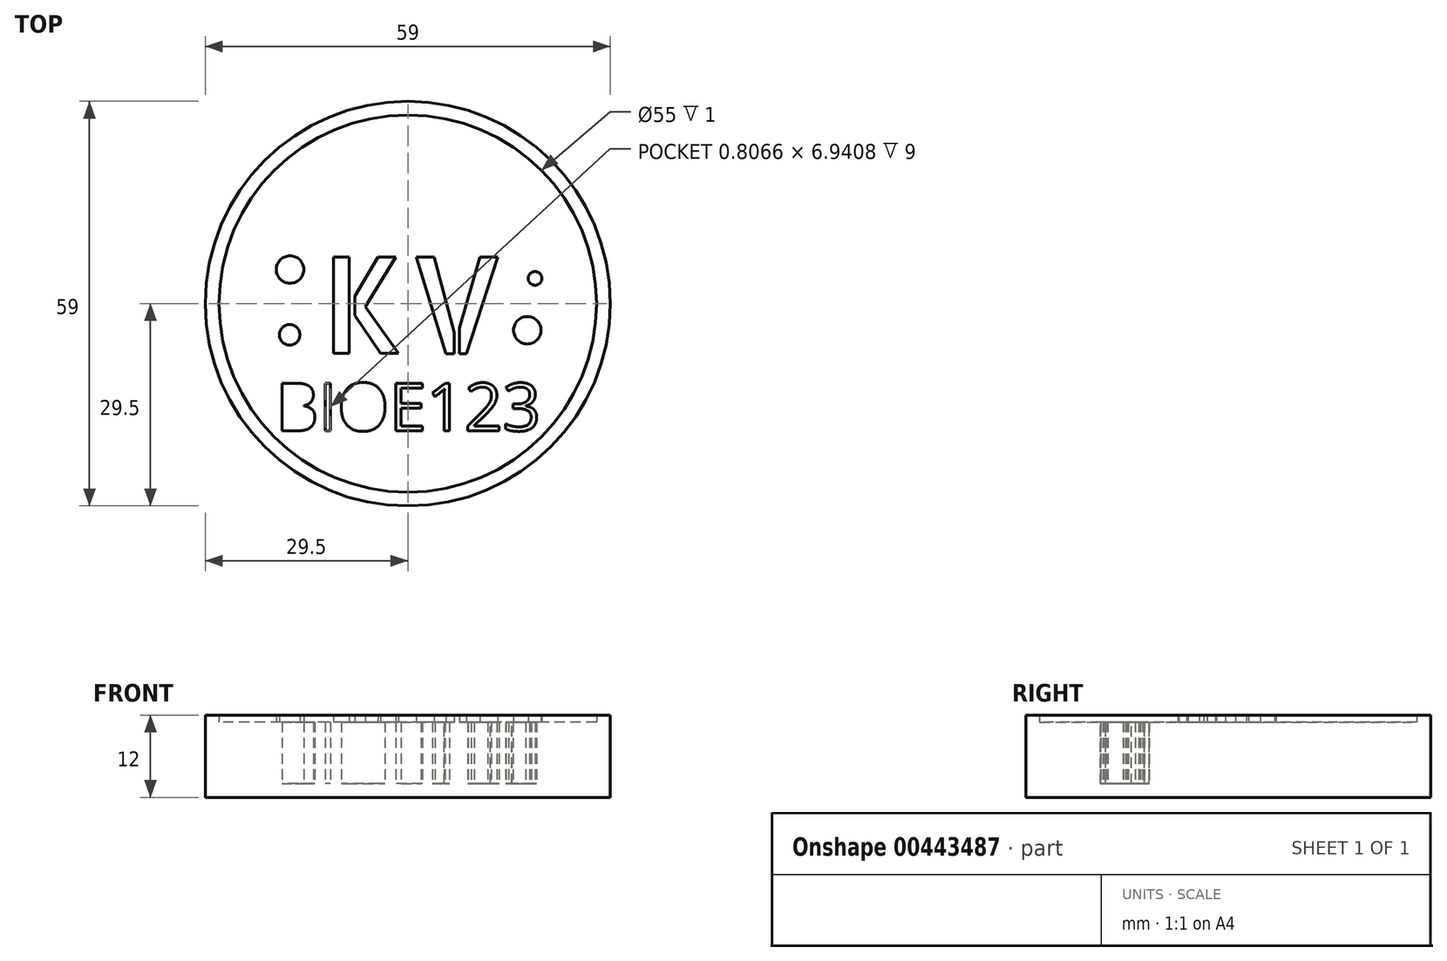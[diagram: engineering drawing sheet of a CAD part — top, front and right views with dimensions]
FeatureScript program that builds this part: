
annotation { "Feature Type Name" : "Feature", "Feature Type Description" : "" }
export const myFeature = defineFeature(function(context is Context, id is Id, definition is map)
    precondition{}
    {
        {
            var Q0;
            Q0=qCreatedBy(makeId("Top.planeOp"),FACE);
            var sketch = newSketch(context, id + "F0", { "sketchPlane" : qUnion([Q0])});
            skCircle(sketch, "E0", {"center": v(0, 0) * mm, "radius": 22.5 * mm});
            skCircle(sketch, "E1", {"center": v(0, 0) * mm, "radius": 27.5 * mm});
            skText(sketch, "E2", { "text": "KV", "fontName": "AllertaStencil-Regular.ttf"});
            skCircle(sketch, "E3", {"center": v(-17.22, -4.56) * mm, "radius": 1.5 * mm});
            skCircle(sketch, "E4", {"center": v(-17.16, 4.97) * mm, "radius": 2 * mm});
            skCircle(sketch, "E5", {"center": v(18.54, 3.68) * mm, "radius": 1 * mm});
            skCircle(sketch, "E6", {"center": v(17.42, -3.88) * mm, "radius": 2 * mm});
            const initialGuessF0  = {"E2": [-0.0126, -0.00722, 1, 0, 0.014]};
            skSetInitialGuess(sketch, initialGuessF0);
            skSolve(sketch);
        }
        {
            var Q0;
            Q0=makeQuery(id+"F0.imprint","IMPRINT",FACE,{"disambiguationData":[TD([[makeQuery(id+"F0.imprint","IMPRINT",EDGE,{"derivedFrom":sQuery(id+"F0.wireOp",EDGE,"E0")}),1.0]])]});
            var Q1;
            Q1=makeQuery(id+"F0.imprint","IMPRINT",FACE,{"disambiguationData":[TD([[makeQuery(id+"F0.imprint","IMPRINT",EDGE,{"derivedFrom":sQuery(id+"F0.wireOp",EDGE,"E0")}),-1.0]])]});
            extrude(context, id + "F1", {"entities" : qUnion([Q0, Q1]), "depth" : 10 * mm});
        }
        {
            var Q0;
            Q0=makeQuery(id+"F1.opExtrude","CAP_FACE",FACE,{"disambiguationData":[OSD([sQuery(id+"F0.wireOp",EDGE,"E1"),sQuery(id+"F0.wireOp",EDGE,"E2.sketch_text.stroke-0"),sQuery(id+"F0.wireOp",EDGE,"E2.sketch_text.stroke-1"),sQuery(id+"F0.wireOp",EDGE,"E2.sketch_text.stroke-2"),sQuery(id+"F0.wireOp",EDGE,"E2.sketch_text.stroke-3"),sQuery(id+"F0.wireOp",EDGE,"E2.sketch_text.stroke-4"),sQuery(id+"F0.wireOp",EDGE,"E2.sketch_text.stroke-5"),sQuery(id+"F0.wireOp",EDGE,"E2.sketch_text.stroke-6"),sQuery(id+"F0.wireOp",EDGE,"E2.sketch_text.stroke-7"),sQuery(id+"F0.wireOp",EDGE,"E2.sketch_text.stroke-8"),sQuery(id+"F0.wireOp",EDGE,"E2.sketch_text.stroke-9"),sQuery(id+"F0.wireOp",EDGE,"E2.sketch_text.stroke-10"),sQuery(id+"F0.wireOp",EDGE,"E2.sketch_text.stroke-11"),sQuery(id+"F0.wireOp",EDGE,"E2.sketch_text.stroke-12"),sQuery(id+"F0.wireOp",EDGE,"E2.sketch_text.stroke-13"),sQuery(id+"F0.wireOp",EDGE,"E2.sketch_text.stroke-14"),sQuery(id+"F0.wireOp",EDGE,"E2.sketch_text.stroke-15"),sQuery(id+"F0.wireOp",EDGE,"E2.sketch_text.stroke-16"),sQuery(id+"F0.wireOp",EDGE,"E2.sketch_text.stroke-17"),sQuery(id+"F0.wireOp",EDGE,"E2.sketch_text.stroke-18"),sQuery(id+"F0.wireOp",EDGE,"E2.sketch_text.stroke-19"),sQuery(id+"F0.wireOp",EDGE,"E2.sketch_text.stroke-20"),sQuery(id+"F0.wireOp",EDGE,"e6WltjxJ-sXpH-rUbf-yrl8-EhS9tpwdPLk9"),sQuery(id+"F0.wireOp",EDGE,"uBJvhWQ7-q3be-jtow-uBxT-aqDe0kTnQ8rm"),sQuery(id+"F0.wireOp",EDGE,"E3"),sQuery(id+"F0.wireOp",EDGE,"E4"),sQuery(id+"F0.wireOp",EDGE,"E5"),sQuery(id+"F0.wireOp",EDGE,"E6"),sQuery(id+"F0.wireOp",EDGE,"PkprW6g8-rJvx-am8A-0Hef-pjwEfByTvvIZ"),sQuery(id+"F0.wireOp",EDGE,"kxHBccSA-AmCE-09R5-Auuk-O76QAIPBnOYI")])],"isStart":false});
            shell(context, id + "F2", {"entities" : qUnion([Q0]), "thickness" : 2 * mm, "oppositeDirection" : true});
        }
        {
            var Q0;
            {var subQ0=sQuery(id+"F0.wireOp",EDGE,"E6");var subQ1=sQuery(id+"F0.wireOp",EDGE,"E5");var subQ2=sQuery(id+"F0.wireOp",EDGE,"E4");var subQ3=sQuery(id+"F0.wireOp",EDGE,"E3");var subQ4=sQuery(id+"F0.wireOp",EDGE,"E2.sketch_text.stroke-20");var subQ5=sQuery(id+"F0.wireOp",EDGE,"E2.sketch_text.stroke-19");var subQ6=sQuery(id+"F0.wireOp",EDGE,"E2.sketch_text.stroke-18");var subQ7=sQuery(id+"F0.wireOp",EDGE,"E2.sketch_text.stroke-17");var subQ8=sQuery(id+"F0.wireOp",EDGE,"E2.sketch_text.stroke-16");var subQ9=sQuery(id+"F0.wireOp",EDGE,"E2.sketch_text.stroke-15");var subQ10=sQuery(id+"F0.wireOp",EDGE,"E2.sketch_text.stroke-14");var subQ11=sQuery(id+"F0.wireOp",EDGE,"E2.sketch_text.stroke-13");var subQ12=sQuery(id+"F0.wireOp",EDGE,"E2.sketch_text.stroke-12");var subQ13=sQuery(id+"F0.wireOp",EDGE,"E2.sketch_text.stroke-11");var subQ14=sQuery(id+"F0.wireOp",EDGE,"E2.sketch_text.stroke-10");var subQ15=sQuery(id+"F0.wireOp",EDGE,"E2.sketch_text.stroke-9");var subQ16=sQuery(id+"F0.wireOp",EDGE,"E2.sketch_text.stroke-8");var subQ17=sQuery(id+"F0.wireOp",EDGE,"E2.sketch_text.stroke-7");var subQ18=sQuery(id+"F0.wireOp",EDGE,"E2.sketch_text.stroke-6");var subQ19=sQuery(id+"F0.wireOp",EDGE,"E2.sketch_text.stroke-5");var subQ20=sQuery(id+"F0.wireOp",EDGE,"E2.sketch_text.stroke-4");var subQ21=sQuery(id+"F0.wireOp",EDGE,"E2.sketch_text.stroke-3");var subQ22=sQuery(id+"F0.wireOp",EDGE,"E2.sketch_text.stroke-2");var subQ23=sQuery(id+"F0.wireOp",EDGE,"E2.sketch_text.stroke-1");var subQ24=sQuery(id+"F0.wireOp",EDGE,"E2.sketch_text.stroke-0");var subQ25=sQuery(id+"F0.wireOp",EDGE,"E1");Q0=makeQuery(id+"F2.opShell","OFFSET_FACE",FACE,{"disambiguationData":[OSD([subQ25,subQ24,subQ23,subQ22,subQ21,subQ20,subQ19,subQ18,subQ17,subQ16,subQ15,subQ14,subQ13,subQ12,subQ11,subQ10,subQ9,subQ8,subQ7,subQ6,subQ5,subQ4,subQ3,subQ2,subQ1,subQ0]),TDD([makeQuery(id+"F1.opExtrude","CAP_FACE",FACE,{"disambiguationData":[OSD([subQ25,subQ24,subQ23,subQ22,subQ21,subQ20,subQ19,subQ18,subQ17,subQ16,subQ15,subQ14,subQ13,subQ12,subQ11,subQ10,subQ9,subQ8,subQ7,subQ6,subQ5,subQ4,subQ3,subQ2,subQ1,subQ0])],"isStart":true})])]});}
            var sketch = newSketch(context, id + "F3", { "sketchPlane" : qUnion([Q0])});
            skText(sketch, "E7", { "text": "BIOE123", "fontName": "OpenSans-Regular.ttf"});
            const initialGuessF3  = {"E7": [-0.0193, -0.01855, 1, 0, 0.007]};
            skSetInitialGuess(sketch, initialGuessF3);
            skSolve(sketch);
        }
        {
            var Q0;
            {var subQ15=sQuery(id+"F0.wireOp",EDGE,"E1");Q0=makeQuery(id+"F3.imprint","IMPRINT",FACE,{"disambiguationData":[TD([[makeQuery(id+"F3.imprint","IMPRINT",EDGE,{"derivedFrom":makeQuery(id+"F2.opShell","OFFSET_EDGE",EDGE,{"disambiguationData":[OSD([subQ15]),TDD([makeQuery(id+"F1.opExtrude","CAP_EDGE",EDGE,{"disambiguationData":[OSD([subQ15])],"isStart":true})])]})}),1.0]])]});}
            extrude(context, id + "F4", {"entities" : qUnion([Q0]), "operationType" : NewBodyOperationType.ADD, "depth" : 9 * mm});
        }
    });
